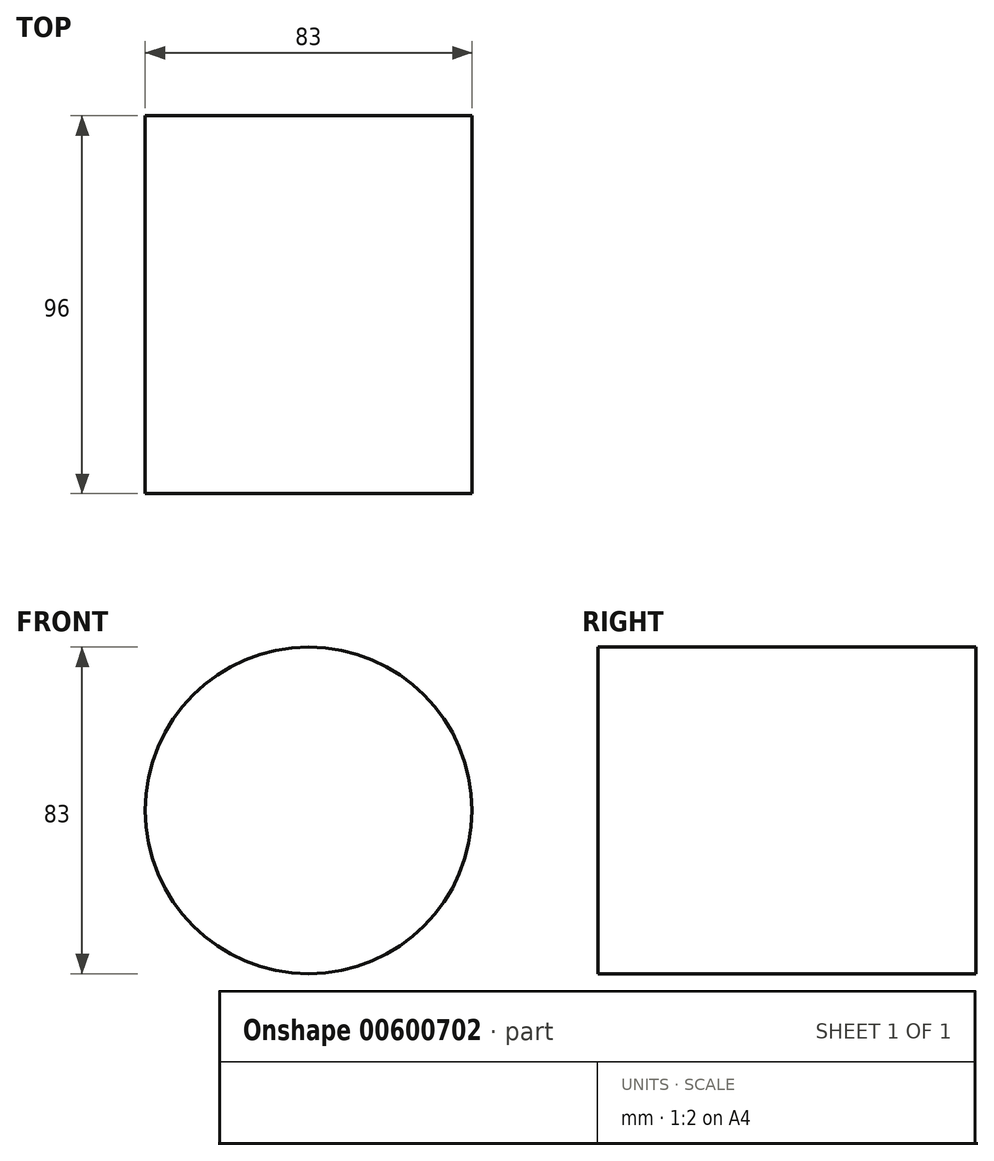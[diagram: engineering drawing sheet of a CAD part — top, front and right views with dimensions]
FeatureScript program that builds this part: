
annotation { "Feature Type Name" : "Feature", "Feature Type Description" : "" }
export const myFeature = defineFeature(function(context is Context, id is Id, definition is map)
    precondition{}
    {
        {
            var Q0;
            Q0=qCreatedBy(makeId("Front.planeOp"),FACE);
            var sketch = newSketch(context, id + "F0", { "sketchPlane" : qUnion([Q0])});
            skCircle(sketch, "E0", {"center": v(0, 0) * mm, "radius": 41.5 * mm});
            skSolve(sketch);
        }
        {
            var Q0;
            Q0=makeQuery(id+"F0.imprint","IMPRINT",FACE,{"disambiguationData":[TD([[makeQuery(id+"F0.imprint","IMPRINT",EDGE,{"derivedFrom":sQuery(id+"F0.wireOp",EDGE,"E0")}),1.0]])]});
            extrude(context, id + "F1", {"entities" : qUnion([Q0]), "depth" : 96 * mm, "offsetDistance" : 25 * mm});
        }
    });
